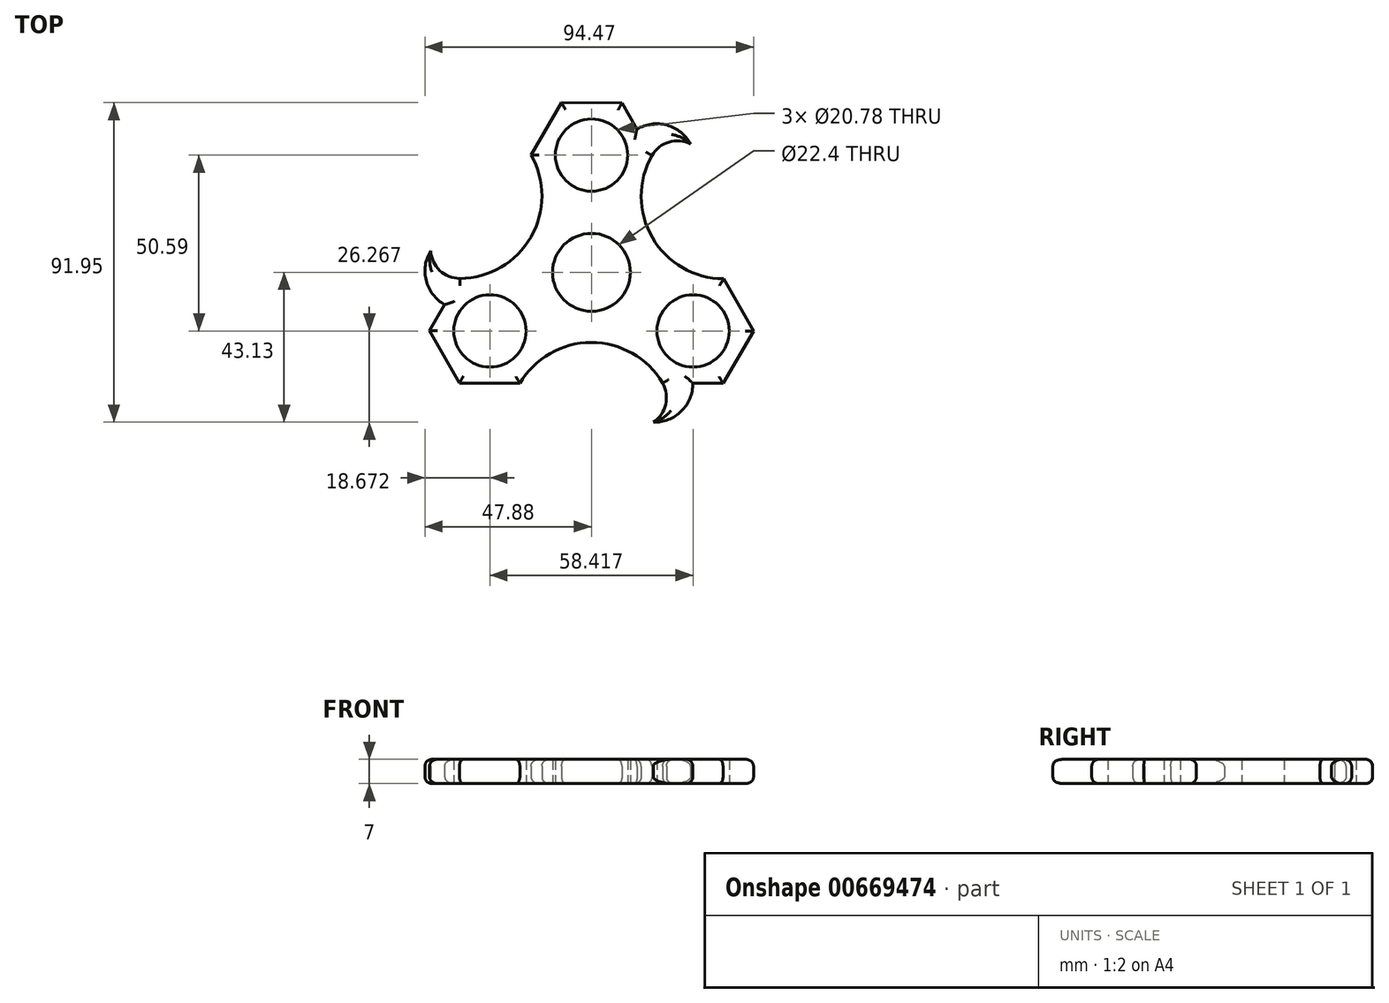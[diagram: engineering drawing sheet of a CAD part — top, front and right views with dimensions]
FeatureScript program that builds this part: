
annotation { "Feature Type Name" : "Feature", "Feature Type Description" : "" }
export const myFeature = defineFeature(function(context is Context, id is Id, definition is map)
    precondition{}
    {
        {
            var Q0;
            Q0=qCreatedBy(makeId("Top.planeOp"),FACE);
            var sketch = newSketch(context, id + "F0", { "sketchPlane" : qUnion([Q0])});
            skCircle(sketch, "E0", {"center": v(0, 0) * mm, "radius": 11.2 * mm});
            skCircle(sketch, "E1", {"center": v(0, 0) * mm, "radius": 13.2 * mm});
            skCircle(sketch, "E2", {"center": v(0, 33.73) * mm, "radius": 10.4 * mm});
            skCircle(sketch, "E3.cCircle", {"center": v(0, 33.73) * mm, "radius": 15.05 * mm, "construction": true});
            skLineSegment(sketch, "E3.0", {"start": v(-17.38, 33.82) * mm, "end": v(-8.61, 48.82) * mm});
            skLineSegment(sketch, "E3.1", {"start": v(-8.61, 48.82) * mm, "end": v(8.77, 48.73) * mm});
            skLineSegment(sketch, "E3.2", {"start": v(8.77, 48.73) * mm, "end": v(17.38, 33.64) * mm});
            skLineSegment(sketch, "E3.3", {"start": v(17.38, 33.64) * mm, "end": v(8.61, 18.63) * mm});
            skLineSegment(sketch, "E3.4", {"start": v(8.61, 18.63) * mm, "end": v(-8.77, 18.72) * mm});
            skLineSegment(sketch, "E3.5", {"start": v(-8.77, 18.72) * mm, "end": v(-17.38, 33.82) * mm});
            skPoint(sketch, "E3.0.midPoint", {"position": v(-13, 41.32) * mm});
            skLineSegment(sketch, "E4.1.0", {"start": v(-37.82, -1.77) * mm, "end": v(-20.44, -1.86) * mm});
            skLineSegment(sketch, "E4.1.1", {"start": v(-46.59, -16.77) * mm, "end": v(-37.82, -1.77) * mm});
            skLineSegment(sketch, "E4.2.0", {"start": v(20.44, -31.87) * mm, "end": v(11.83, -16.77) * mm});
            skLineSegment(sketch, "E4.2.1", {"start": v(37.82, -31.96) * mm, "end": v(20.44, -31.87) * mm});
            skLineSegment(sketch, "E5.1.1", {"start": v(-20.44, -1.86) * mm, "end": v(-11.83, -16.95) * mm});
            skLineSegment(sketch, "E5.1.3", {"start": v(-11.83, -16.95) * mm, "end": v(-20.6, -31.96) * mm});
            skLineSegment(sketch, "E5.1.4", {"start": v(-20.6, -31.96) * mm, "end": v(-37.98, -31.87) * mm});
            skLineSegment(sketch, "E5.2.1", {"start": v(11.83, -16.77) * mm, "end": v(20.6, -1.77) * mm});
            skLineSegment(sketch, "E5.2.3", {"start": v(20.6, -1.77) * mm, "end": v(37.98, -1.86) * mm});
            skLineSegment(sketch, "E5.2.4", {"start": v(37.98, -1.86) * mm, "end": v(46.59, -16.95) * mm});
            skLineSegment(sketch, "E6.1.0", {"start": v(-37.98, -31.87) * mm, "end": v(-46.59, -16.77) * mm});
            skCircle(sketch, "E6.1.1", {"center": v(-29.2, -16.86) * mm, "radius": 10.4 * mm});
            skCircle(sketch, "E6.1.2", {"center": v(-29.2, -16.86) * mm, "radius": 15.05 * mm, "construction": true});
            skLineSegment(sketch, "E6.2.0", {"start": v(46.59, -16.95) * mm, "end": v(37.82, -31.96) * mm});
            skCircle(sketch, "E6.2.1", {"center": v(29.2, -16.86) * mm, "radius": 10.4 * mm});
            skCircle(sketch, "E6.2.2", {"center": v(29.2, -16.86) * mm, "radius": 15.05 * mm, "construction": true});
            skArc(sketch, "E7", {"start": v(-37.82, -1.77) * mm, "mid": v(-17.41, 10.17) * mm, "end": v(-17.38, 33.82) * mm});
            skArc(sketch, "E8.1.0", {"start": v(20.44, -31.87) * mm, "mid": v(-0.1, -20.17) * mm, "end": v(-20.6, -31.96) * mm});
            skArc(sketch, "E8.2.0", {"start": v(17.38, 33.64) * mm, "mid": v(17.52, 10) * mm, "end": v(37.98, -1.86) * mm});
            skArc(sketch, "E9", {"start": v(28.47, 36.94) * mm, "mid": v(21.68, 42.36) * mm, "end": v(13.07, 41.18) * mm});
            skArc(sketch, "E10", {"start": v(28.47, 36.94) * mm, "mid": v(22.27, 37.48) * mm, "end": v(17.38, 33.64) * mm});
            skArc(sketch, "E11.1.0", {"start": v(-46.23, 6.19) * mm, "mid": v(-47.52, -2.4) * mm, "end": v(-42.2, -9.27) * mm});
            skArc(sketch, "E11.1.1", {"start": v(-46.23, 6.19) * mm, "mid": v(-43.6, 0.55) * mm, "end": v(-37.82, -1.77) * mm});
            skArc(sketch, "E11.2.0", {"start": v(17.75, -43.13) * mm, "mid": v(25.84, -39.96) * mm, "end": v(29.13, -31.91) * mm});
            skArc(sketch, "E11.2.1", {"start": v(17.75, -43.13) * mm, "mid": v(21.32, -38.03) * mm, "end": v(20.44, -31.87) * mm});
            skSolve(sketch);
        }
        {
            var Q0;
            Q0=makeQuery(id+"F0.imprint","IMPRINT",FACE,{"disambiguationData":[TD([[makeQuery(id+"F0.imprint","IMPRINT",EDGE,{"derivedFrom":sQuery(id+"F0.wireOp",EDGE,"E1")}),-1.0]])]});
            var Q1;
            Q1=makeQuery(id+"F0.imprint","IMPRINT",FACE,{"disambiguationData":[TD([[makeQuery(id+"F0.imprint","IMPRINT",EDGE,{"derivedFrom":sQuery(id+"F0.wireOp",EDGE,"E5.1.1")}),-1.0]])]});
            var Q2;
            {var subQ2=sQuery(id+"F0.wireOp",EDGE,"E11.1.0");Q2=makeQuery(id+"F0.imprint","IMPRINT",FACE,{"disambiguationData":[TD([[makeQuery(id+"F0.imprint","IMPRINT",EDGE,{"derivedFrom":subQ2}),1.0]])]});}
            var Q3;
            Q3=makeQuery(id+"F0.imprint","IMPRINT",FACE,{"disambiguationData":[TD([[makeQuery(id+"F0.imprint","IMPRINT",EDGE,{"derivedFrom":sQuery(id+"F0.wireOp",EDGE,"E2")}),-1.0]])]});
            var Q4;
            {var subQ2=sQuery(id+"F0.wireOp",EDGE,"E9");Q4=makeQuery(id+"F0.imprint","IMPRINT",FACE,{"disambiguationData":[TD([[makeQuery(id+"F0.imprint","IMPRINT",EDGE,{"derivedFrom":subQ2}),1.0]])]});}
            var Q5;
            Q5=makeQuery(id+"F0.imprint","IMPRINT",FACE,{"disambiguationData":[TD([[makeQuery(id+"F0.imprint","IMPRINT",EDGE,{"derivedFrom":sQuery(id+"F0.wireOp",EDGE,"E5.2.1")}),-1.0]])]});
            var Q6;
            {var subQ2=sQuery(id+"F0.wireOp",EDGE,"E11.2.0");Q6=makeQuery(id+"F0.imprint","IMPRINT",FACE,{"disambiguationData":[TD([[makeQuery(id+"F0.imprint","IMPRINT",EDGE,{"derivedFrom":subQ2}),1.0]])]});}
            var Q7;
            Q7=makeQuery(id+"F0.imprint","IMPRINT",FACE,{"disambiguationData":[TD([[makeQuery(id+"F0.imprint","IMPRINT",EDGE,{"derivedFrom":sQuery(id+"F0.wireOp",EDGE,"E0")}),-1.0]])]});
            extrude(context, id + "F1", {"entities" : qUnion([Q0, Q1, Q2, Q3, Q4, Q5, Q6, Q7]), "depth" : 7 * mm, "offsetDistance" : 25 * mm});
        }
        {
            var Q0;
            Q0=makeQuery(id+"F1.opExtrude","CAP_EDGE",EDGE,{"disambiguationData":[OSD([sQuery(id+"F0.wireOp",EDGE,"E8.1.0")])],"isStart":false});
            var Q1;
            Q1=makeQuery(id+"F1.opExtrude","CAP_EDGE",EDGE,{"disambiguationData":[OSD([sQuery(id+"F0.wireOp",EDGE,"E8.2.0")])],"isStart":false});
            var Q2;
            Q2=makeQuery(id+"F1.opExtrude","CAP_EDGE",EDGE,{"disambiguationData":[OSD([sQuery(id+"F0.wireOp",EDGE,"E7")])],"isStart":false});
            var Q3;
            Q3=makeQuery(id+"F1.opExtrude","CAP_EDGE",EDGE,{"disambiguationData":[OSD([sQuery(id+"F0.wireOp",EDGE,"E11.1.0")])],"isStart":false});
            var Q4;
            Q4=makeQuery(id+"F1.opExtrude","CAP_EDGE",EDGE,{"disambiguationData":[OSD([sQuery(id+"F0.wireOp",EDGE,"E4.1.1")])],"isStart":false});
            var Q5;
            Q5=makeQuery(id+"F1.opExtrude","CAP_EDGE",EDGE,{"disambiguationData":[OSD([sQuery(id+"F0.wireOp",EDGE,"E5.1.4")])],"isStart":false});
            var Q6;
            Q6=makeQuery(id+"F1.opExtrude","CAP_EDGE",EDGE,{"disambiguationData":[OSD([sQuery(id+"F0.wireOp",EDGE,"E6.1.0")])],"isStart":false});
            var Q7;
            Q7=makeQuery(id+"F1.opExtrude","CAP_EDGE",EDGE,{"disambiguationData":[OSD([sQuery(id+"F0.wireOp",EDGE,"E11.2.0")])],"isStart":false});
            var Q8;
            Q8=makeQuery(id+"F1.opExtrude","CAP_EDGE",EDGE,{"disambiguationData":[OSD([sQuery(id+"F0.wireOp",EDGE,"E6.2.0")])],"isStart":false});
            var Q9;
            Q9=makeQuery(id+"F1.opExtrude","CAP_EDGE",EDGE,{"disambiguationData":[OSD([sQuery(id+"F0.wireOp",EDGE,"E4.2.1")])],"isStart":false});
            var Q10;
            Q10=makeQuery(id+"F1.opExtrude","CAP_EDGE",EDGE,{"disambiguationData":[OSD([sQuery(id+"F0.wireOp",EDGE,"E5.2.4")])],"isStart":false});
            var Q11;
            Q11=makeQuery(id+"F1.opExtrude","CAP_EDGE",EDGE,{"disambiguationData":[OSD([sQuery(id+"F0.wireOp",EDGE,"E9")])],"isStart":false});
            var Q12;
            Q12=makeQuery(id+"F1.opExtrude","CAP_EDGE",EDGE,{"disambiguationData":[OSD([sQuery(id+"F0.wireOp",EDGE,"E3.1")])],"isStart":false});
            var Q13;
            Q13=makeQuery(id+"F1.opExtrude","CAP_EDGE",EDGE,{"disambiguationData":[OSD([sQuery(id+"F0.wireOp",EDGE,"E3.2")])],"isStart":false});
            var Q14;
            Q14=makeQuery(id+"F1.opExtrude","CAP_EDGE",EDGE,{"disambiguationData":[OSD([sQuery(id+"F0.wireOp",EDGE,"E3.0")])],"isStart":false});
            fillet(context, id + "F2", {"entities" : qUnion([Q0, Q1, Q2, Q3, Q4, Q5, Q6, Q7, Q8, Q9, Q10, Q11, Q12, Q13, Q14]), "radius" : 2 * mm, "tangentPropagation" : true, "allowEdgeOverflow" : false});
        }
        {
            var Q0;
            Q0=makeQuery(id+"F1.opExtrude","CAP_EDGE",EDGE,{"disambiguationData":[OSD([sQuery(id+"F0.wireOp",EDGE,"E4.1.1")])],"isStart":true});
            var Q1;
            Q1=makeQuery(id+"F1.opExtrude","CAP_EDGE",EDGE,{"disambiguationData":[OSD([sQuery(id+"F0.wireOp",EDGE,"E6.1.0")])],"isStart":true});
            var Q2;
            Q2=makeQuery(id+"F1.opExtrude","CAP_EDGE",EDGE,{"disambiguationData":[OSD([sQuery(id+"F0.wireOp",EDGE,"E11.1.0")])],"isStart":true});
            var Q3;
            Q3=makeQuery(id+"F1.opExtrude","CAP_EDGE",EDGE,{"disambiguationData":[OSD([sQuery(id+"F0.wireOp",EDGE,"E7")])],"isStart":true});
            var Q4;
            Q4=makeQuery(id+"F1.opExtrude","CAP_EDGE",EDGE,{"disambiguationData":[OSD([sQuery(id+"F0.wireOp",EDGE,"E3.0")])],"isStart":true});
            var Q5;
            Q5=makeQuery(id+"F1.opExtrude","CAP_EDGE",EDGE,{"disambiguationData":[OSD([sQuery(id+"F0.wireOp",EDGE,"E3.1")])],"isStart":true});
            var Q6;
            Q6=makeQuery(id+"F1.opExtrude","CAP_EDGE",EDGE,{"disambiguationData":[OSD([sQuery(id+"F0.wireOp",EDGE,"E9")])],"isStart":true});
            var Q7;
            Q7=makeQuery(id+"F1.opExtrude","CAP_EDGE",EDGE,{"disambiguationData":[OSD([sQuery(id+"F0.wireOp",EDGE,"E3.2")])],"isStart":true});
            var Q8;
            Q8=makeQuery(id+"F1.opExtrude","CAP_EDGE",EDGE,{"disambiguationData":[OSD([sQuery(id+"F0.wireOp",EDGE,"E8.2.0")])],"isStart":true});
            var Q9;
            Q9=makeQuery(id+"F1.opExtrude","CAP_EDGE",EDGE,{"disambiguationData":[OSD([sQuery(id+"F0.wireOp",EDGE,"E5.2.4")])],"isStart":true});
            var Q10;
            Q10=makeQuery(id+"F1.opExtrude","CAP_EDGE",EDGE,{"disambiguationData":[OSD([sQuery(id+"F0.wireOp",EDGE,"E6.2.0")])],"isStart":true});
            var Q11;
            Q11=makeQuery(id+"F1.opExtrude","CAP_EDGE",EDGE,{"disambiguationData":[OSD([sQuery(id+"F0.wireOp",EDGE,"E4.2.1")])],"isStart":true});
            var Q12;
            Q12=makeQuery(id+"F1.opExtrude","CAP_EDGE",EDGE,{"disambiguationData":[OSD([sQuery(id+"F0.wireOp",EDGE,"E11.2.0")])],"isStart":true});
            var Q13;
            Q13=makeQuery(id+"F1.opExtrude","CAP_EDGE",EDGE,{"disambiguationData":[OSD([sQuery(id+"F0.wireOp",EDGE,"E8.1.0")])],"isStart":true});
            var Q14;
            Q14=makeQuery(id+"F1.opExtrude","CAP_EDGE",EDGE,{"disambiguationData":[OSD([sQuery(id+"F0.wireOp",EDGE,"E5.1.4")])],"isStart":true});
            fillet(context, id + "F3", {"entities" : qUnion([Q0, Q1, Q2, Q3, Q4, Q5, Q6, Q7, Q8, Q9, Q10, Q11, Q12, Q13, Q14]), "radius" : 2 * mm, "tangentPropagation" : true, "allowEdgeOverflow" : false});
        }
    });
